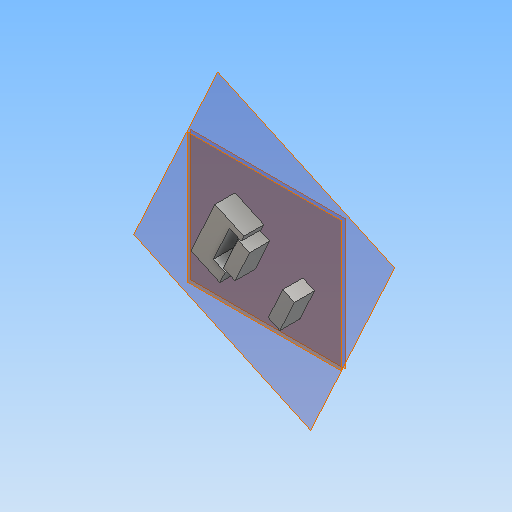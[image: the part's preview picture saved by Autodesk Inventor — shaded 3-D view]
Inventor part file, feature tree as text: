
AUTODESK INVENTOR PART (.ipt)
format: ipt  version: 2019.4 (Build 234330000, 330)  size: 121,856 bytes
history: native  units: mm
features: plane x3, extrude x2, sketch x2, other x2, reference x1
ambient origin geometry x8: Origin, YZ Plane, XZ Plane, XY Plane, X Axis, Y Axis, Z Axis, Center Point
bodies: Solid1 (feature_tree)
feature tree (10):
  plane  "Work Plane1"
  plane  "Work Plane2"
  extrude  "Extrusion1"  Depth=3.5mm
  plane  "Work Plane3"
  extrude  "Extrusion2"  Depth=3.5mm
  sketch  "Sketch1"  dims[d0=9.5mm d1=3.5mm]
  reference  "Reference1"
  sketch  "Sketch2"  dims[d2=9.5mm d3=3.5mm d4=0.0mm d5=2.5mm d6=10.0mm d7=0.0mm d8=5.5mm d9=0.0mm d10=5.5mm d11=0.0mm]
  other  "00_KES400.iam"
  other  "00_KES400_Bluray_Lens:1"
